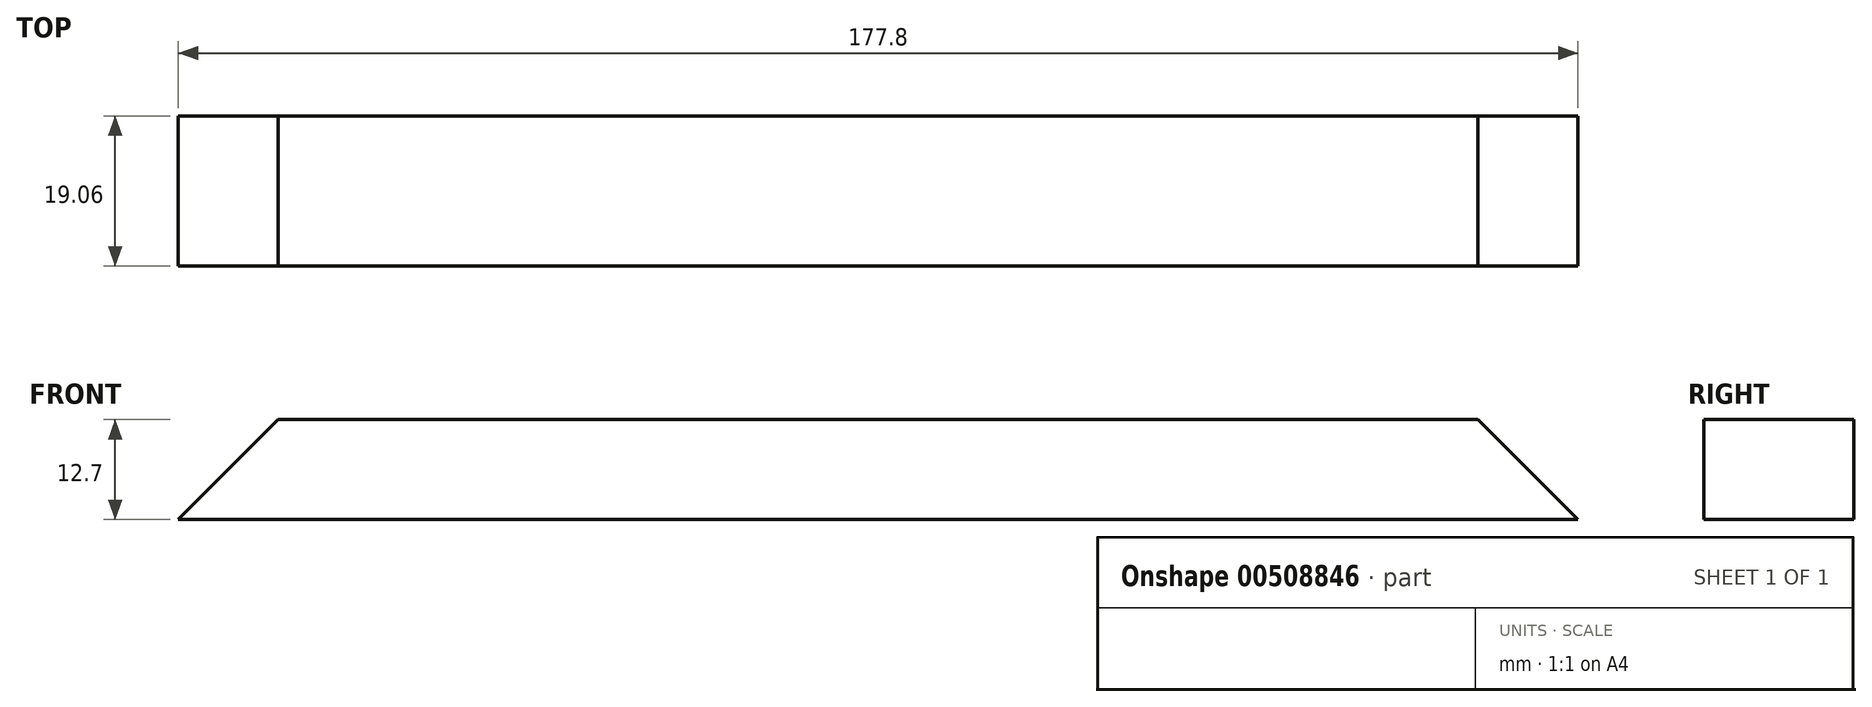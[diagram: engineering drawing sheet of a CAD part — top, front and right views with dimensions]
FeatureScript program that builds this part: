
annotation { "Feature Type Name" : "Feature", "Feature Type Description" : "" }
export const myFeature = defineFeature(function(context is Context, id is Id, definition is map)
    precondition{}
    {
        {
            var Q0;
            Q0=qCreatedBy(makeId("Front.planeOp"),FACE);
            var sketch = newSketch(context, id + "F0", { "sketchPlane" : qUnion([Q0])});
            skLineSegment(sketch, "E0.bottom", {"start": v(76.2, 6.35) * mm, "end": v(-76.2, 6.35) * mm});
            skLineSegment(sketch, "E0.top", {"start": v(88.9, -6.35) * mm, "end": v(-88.9, -6.35) * mm});
            skPoint(sketch, "E0.middle", {"position": v(0, 0) * mm});
            skLineSegment(sketch, "E1", {"start": v(-88.9, -6.35) * mm, "end": v(-76.2, 6.35) * mm});
            skLineSegment(sketch, "E2", {"start": v(88.9, -6.35) * mm, "end": v(76.2, 6.35) * mm});
            skSolve(sketch);
        }
        {
            var Q0;
            Q0=makeQuery(id+"F0.imprint","IMPRINT",FACE,{"disambiguationData":[TD([[makeQuery(id+"F0.imprint","IMPRINT",EDGE,{"derivedFrom":sQuery(id+"F0.wireOp",EDGE,"E0.bottom")}),1.0]])]});
            extrude(context, id + "F1", {"entities" : qUnion([Q0]), "endBound" : BoundingType.SYMMETRIC, "depth" : 19.05 * mm});
        }
    });
